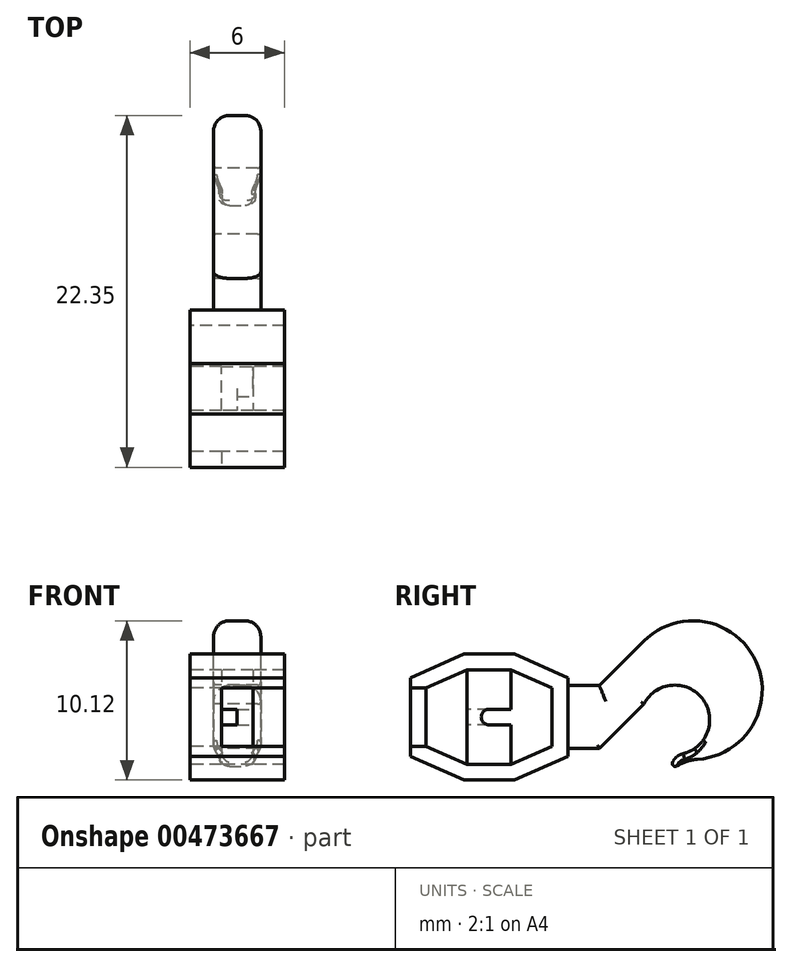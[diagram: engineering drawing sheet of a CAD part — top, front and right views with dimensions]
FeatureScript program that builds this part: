
annotation { "Feature Type Name" : "Feature", "Feature Type Description" : "" }
export const myFeature = defineFeature(function(context is Context, id is Id, definition is map)
    precondition{}
    {
        {
            var Q0;
            Q0=qCreatedBy(makeId("Right.planeOp"),FACE);
            var sketch = newSketch(context, id + "F0", { "sketchPlane" : qUnion([Q0])});
            skLineSegment(sketch, "E0", {"start": v(0, 0) * mm, "end": v(0, 4) * mm, "construction": true});
            skLineSegment(sketch, "E1", {"start": v(0, 0) * mm, "end": v(5, 0) * mm, "construction": true});
            skLineSegment(sketch, "E2", {"start": v(0, 4) * mm, "end": v(1.6, 4) * mm});
            skLineSegment(sketch, "E3", {"start": v(5, 0) * mm, "end": v(5, 2.5) * mm});
            skLineSegment(sketch, "E4", {"start": v(1.6, 4) * mm, "end": v(5, 2.5) * mm});
            skLineSegment(sketch, "E5.MirrorCS", {"start": v(0, 4) * mm, "end": v(-1.6, 4) * mm});
            skLineSegment(sketch, "E6.MirrorCS", {"start": v(-1.6, 4) * mm, "end": v(-5, 2.5) * mm});
            skLineSegment(sketch, "E7.MirrorCS", {"start": v(-5, 0) * mm, "end": v(-5, 2.5) * mm});
            skLineSegment(sketch, "E8.MirrorCS", {"start": v(-5, 0) * mm, "end": v(-5, -2.5) * mm});
            skLineSegment(sketch, "E9.MirrorCS", {"start": v(-1.6, -4) * mm, "end": v(-5, -2.5) * mm});
            skLineSegment(sketch, "E10.MirrorCS", {"start": v(0, -4) * mm, "end": v(1.6, -4) * mm});
            skLineSegment(sketch, "E11.MirrorCS", {"start": v(0, -4) * mm, "end": v(-1.6, -4) * mm});
            skLineSegment(sketch, "E12.MirrorCS", {"start": v(1.6, -4) * mm, "end": v(5, -2.5) * mm});
            skLineSegment(sketch, "E13.MirrorCS", {"start": v(5, 0) * mm, "end": v(5, -2.5) * mm});
            skLineSegment(sketch, "E14.0", {"start": v(0, 3) * mm, "end": v(1.39, 3) * mm});
            skLineSegment(sketch, "E14.1", {"start": v(0, -3) * mm, "end": v(1.39, -3) * mm});
            skLineSegment(sketch, "E14.2", {"start": v(1.39, -3) * mm, "end": v(4, -1.85) * mm});
            skLineSegment(sketch, "E14.3", {"start": v(4, 0) * mm, "end": v(4, -1.85) * mm});
            skLineSegment(sketch, "E14.4", {"start": v(4, 0) * mm, "end": v(4, 1.85) * mm});
            skLineSegment(sketch, "E14.5", {"start": v(0, -3) * mm, "end": v(-1.39, -3) * mm});
            skLineSegment(sketch, "E14.6", {"start": v(1.39, 3) * mm, "end": v(4, 1.85) * mm});
            skLineSegment(sketch, "E14.7", {"start": v(-1.39, -3) * mm, "end": v(-4, -1.85) * mm});
            skLineSegment(sketch, "E14.8", {"start": v(-4, 0) * mm, "end": v(-4, -1.85) * mm});
            skLineSegment(sketch, "E14.9", {"start": v(-4, 0) * mm, "end": v(-4, 1.85) * mm});
            skLineSegment(sketch, "E14.10", {"start": v(-1.39, 3) * mm, "end": v(-4, 1.85) * mm});
            skLineSegment(sketch, "E14.11", {"start": v(0, 3) * mm, "end": v(-1.39, 3) * mm});
            skSolve(sketch);
        }
        {
            var Q0;
            Q0=makeQuery(id+"F0.imprint","IMPRINT",FACE,{"disambiguationData":[TD([[makeQuery(id+"F0.imprint","IMPRINT",EDGE,{"derivedFrom":sQuery(id+"F0.wireOp",EDGE,"E14.0")}),-1.0]])]});
            var sketch = newSketch(context, id + "F1", { "sketchPlane" : qUnion([Q0])});
            skPoint(sketch, "E15.0", {"position": v(-1.39, 3) * mm});
            skPoint(sketch, "E16.0", {"position": v(1.39, 3) * mm});
            skPoint(sketch, "E17.0", {"position": v(-1.39, -3) * mm});
            skPoint(sketch, "E18.0", {"position": v(1.39, -3) * mm});
            skLineSegment(sketch, "E19.bottom", {"start": v(-1.39, 3) * mm, "end": v(1.39, 3) * mm});
            skLineSegment(sketch, "E19.top", {"start": v(-1.39, -3) * mm, "end": v(1.39, -3) * mm});
            skLineSegment(sketch, "E19.left", {"start": v(-1.39, 3) * mm, "end": v(-1.39, -3) * mm});
            skLineSegment(sketch, "E19.right", {"start": v(1.39, 3) * mm, "end": v(1.39, -3) * mm});
            skSolve(sketch);
        }
        {
            var Q0;
            Q0=qCreatedBy(makeId("Right.planeOp"),FACE);
            var sketch = newSketch(context, id + "F2", { "sketchPlane" : qUnion([Q0])});
            skPoint(sketch, "E20.0", {"position": v(5, 0) * mm});
            skLineSegment(sketch, "E21", {"start": v(5, 0) * mm, "end": v(5, 2) * mm, "construction": true});
            skLineSegment(sketch, "E22.bottom", {"start": v(5, 2) * mm, "end": v(7, 2) * mm});
            skLineSegment(sketch, "E22.top", {"start": v(5, -2) * mm, "end": v(7, -2) * mm});
            skLineSegment(sketch, "E22.left", {"start": v(5, 2) * mm, "end": v(5, -2) * mm});
            skLineSegment(sketch, "E22.right", {"start": v(7, 2) * mm, "end": v(7, -2) * mm});
            skLineSegment(sketch, "E23", {"start": v(5, 0) * mm, "end": v(17, 0) * mm, "construction": true});
            skLineSegment(sketch, "E24", {"start": v(7, 2) * mm, "end": v(9.83, 4.83) * mm});
            skLineSegment(sketch, "E25", {"start": v(7, -2) * mm, "end": v(9.83, 0.83) * mm});
            skArc(sketch, "E26", {"start": v(9.83, 4.83) * mm, "mid": v(15.4, 5.37) * mm, "end": v(17, 0) * mm});
            skLineSegment(sketch, "E27", {"start": v(17, 0) * mm, "end": v(14, 0) * mm, "construction": true});
            skArc(sketch, "E28", {"start": v(14, 0) * mm, "mid": v(12.23, 2) * mm, "end": v(9.83, 0.83) * mm});
            skArc(sketch, "E29", {"start": v(14, 0) * mm, "mid": v(13.58, -1.48) * mm, "end": v(12.3, -2.33) * mm});
            skArc(sketch, "E30", {"start": v(17, 0) * mm, "mid": v(15.5, -1.87) * mm, "end": v(13.25, -2.68) * mm});
            skLineSegment(sketch, "E31", {"start": v(14, 0) * mm, "end": v(13.25, 0) * mm, "construction": true});
            skLineSegment(sketch, "E32", {"start": v(13.25, 0) * mm, "end": v(12.3, 0) * mm, "construction": true});
            skLineSegment(sketch, "E33", {"start": v(13.25, -2.68) * mm, "end": v(13.25, -3.38) * mm, "construction": true});
            skArc(sketch, "E34", {"start": v(12.3, -2.33) * mm, "mid": v(11.73, -2.71) * mm, "end": v(11.56, -3.38) * mm});
            skArc(sketch, "E35", {"start": v(13.25, -2.68) * mm, "mid": v(12.35, -2.9) * mm, "end": v(11.56, -3.38) * mm});
            skLineSegment(sketch, "E36", {"start": v(13.25, -3.38) * mm, "end": v(11.56, -3.38) * mm, "construction": true});
            skSolve(sketch);
        }
        {
            var Q0;
            Q0=makeQuery(id+"F0.imprint","IMPRINT",FACE,{"disambiguationData":[TD([[makeQuery(id+"F0.imprint","IMPRINT",EDGE,{"derivedFrom":sQuery(id+"F0.wireOp",EDGE,"E2")}),-1.0]])]});
            extrude(context, id + "F3", {"entities" : qUnion([Q0]), "endBound" : BoundingType.SYMMETRIC, "depth" : 6 * mm});
        }
        {
            var Q0;
            {var subQ3=sQuery(id+"F1.wireOp",EDGE,"E19.left");Q0=makeQuery(id+"F1.imprint","IMPRINT",FACE,{"disambiguationData":[TD([[makeQuery(id+"F1.imprint","IMPRINT",EDGE,{"derivedFrom":subQ3}),1.0]])]});}
            extrude(context, id + "F4", {"entities" : qUnion([Q0]), "operationType" : NewBodyOperationType.ADD, "endBound" : BoundingType.SYMMETRIC, "depth" : 2 * mm});
        }
        {
            var Q0;
            Q0=makeQuery(id+"F2.imprint","IMPRINT",FACE,{"disambiguationData":[TD([[makeQuery(id+"F2.imprint","IMPRINT",EDGE,{"derivedFrom":sQuery(id+"F2.wireOp",EDGE,"E22.bottom")}),-1.0]])]});
            var Q1;
            Q1=makeQuery(id+"F2.imprint","IMPRINT",FACE,{"disambiguationData":[TD([[makeQuery(id+"F2.imprint","IMPRINT",EDGE,{"derivedFrom":sQuery(id+"F2.wireOp",EDGE,"E22.right")}),1.0]])]});
            extrude(context, id + "F5", {"entities" : qUnion([Q0, Q1]), "operationType" : NewBodyOperationType.ADD, "endBound" : BoundingType.SYMMETRIC, "depth" : 3 * mm});
        }
        {
            var Q0;
            Q0=makeQuery(id+"F3.opExtrude","CAP_FACE",FACE,{"disambiguationData":[OSD([sQuery(id+"F0.wireOp",EDGE,"E2"),sQuery(id+"F0.wireOp",EDGE,"E3"),sQuery(id+"F0.wireOp",EDGE,"E4"),sQuery(id+"F0.wireOp",EDGE,"E5.MirrorCS"),sQuery(id+"F0.wireOp",EDGE,"E6.MirrorCS"),sQuery(id+"F0.wireOp",EDGE,"E7.MirrorCS"),sQuery(id+"F0.wireOp",EDGE,"E8.MirrorCS"),sQuery(id+"F0.wireOp",EDGE,"E9.MirrorCS"),sQuery(id+"F0.wireOp",EDGE,"E10.MirrorCS"),sQuery(id+"F0.wireOp",EDGE,"E11.MirrorCS"),sQuery(id+"F0.wireOp",EDGE,"E12.MirrorCS"),sQuery(id+"F0.wireOp",EDGE,"E13.MirrorCS"),sQuery(id+"F0.wireOp",EDGE,"E14.0"),sQuery(id+"F0.wireOp",EDGE,"E14.1"),sQuery(id+"F0.wireOp",EDGE,"E14.2"),sQuery(id+"F0.wireOp",EDGE,"E14.3"),sQuery(id+"F0.wireOp",EDGE,"E14.4"),sQuery(id+"F0.wireOp",EDGE,"E14.5"),sQuery(id+"F0.wireOp",EDGE,"E14.6"),sQuery(id+"F0.wireOp",EDGE,"E14.7"),sQuery(id+"F0.wireOp",EDGE,"E14.8"),sQuery(id+"F0.wireOp",EDGE,"E14.9"),sQuery(id+"F0.wireOp",EDGE,"E14.10"),sQuery(id+"F0.wireOp",EDGE,"E14.11")])],"isStart":false});
            var sketch = newSketch(context, id + "F6", { "sketchPlane" : qUnion([Q0])});
            skPoint(sketch, "E37.0", {"position": v(-4, 1.85) * mm});
            skPoint(sketch, "E38.0", {"position": v(-5, 2.5) * mm});
            skPoint(sketch, "E39.0", {"position": v(-4, -1.85) * mm});
            skLineSegment(sketch, "E40.bottom", {"start": v(-4, 1.85) * mm, "end": v(-5, 1.85) * mm});
            skLineSegment(sketch, "E40.top", {"start": v(-4, -1.85) * mm, "end": v(-5, -1.85) * mm});
            skLineSegment(sketch, "E40.left", {"start": v(-4, 1.85) * mm, "end": v(-4, -1.85) * mm});
            skLineSegment(sketch, "E40.right", {"start": v(-5, 1.85) * mm, "end": v(-5, -1.85) * mm});
            skSolve(sketch);
        }
        {
            var Q0;
            Q0=makeQuery(id+"F6.imprint","IMPRINT",FACE,{"disambiguationData":[TD([[makeQuery(id+"F6.imprint","IMPRINT",EDGE,{"derivedFrom":sQuery(id+"F6.wireOp",EDGE,"E40.bottom")}),1.0]])]});
            extrude(context, id + "F7", {"entities" : qUnion([Q0]), "operationType" : NewBodyOperationType.REMOVE, "oppositeDirection" : true, "depth" : 4 * mm});
        }
        {
            var Q0;
            Q0=makeQuery(id+"F5.opExtrude","CAP_EDGE",EDGE,{"disambiguationData":[OSD([sQuery(id+"F2.wireOp",EDGE,"E22.bottom")])],"isStart":false});
            var Q1;
            Q1=makeQuery(id+"F5.opExtrude","CAP_EDGE",EDGE,{"disambiguationData":[OSD([sQuery(id+"F2.wireOp",EDGE,"E24")])],"isStart":false});
            var Q2;
            Q2=makeQuery(id+"F5.opExtrude","CAP_EDGE",EDGE,{"disambiguationData":[OSD([sQuery(id+"F2.wireOp",EDGE,"E26"),sQuery(id+"F2.wireOp",EDGE,"E30")])],"isStart":false});
            var Q3;
            Q3=makeQuery(id+"F5.opExtrude","CAP_EDGE",EDGE,{"disambiguationData":[OSD([sQuery(id+"F2.wireOp",EDGE,"E26"),sQuery(id+"F2.wireOp",EDGE,"E30")])],"isStart":true});
            var Q4;
            Q4=makeQuery(id+"F5.opExtrude","CAP_EDGE",EDGE,{"disambiguationData":[OSD([sQuery(id+"F2.wireOp",EDGE,"E22.bottom")])],"isStart":true});
            fillet(context, id + "F8", {"entities" : qUnion([Q0, Q1, Q2, Q3, Q4]), "radius" : 1 * mm, "tangentPropagation" : true, "allowEdgeOverflow" : false});
        }
        {
            var Q0;
            Q0=makeQuery(id+"F5.opExtrude","CAP_EDGE",EDGE,{"disambiguationData":[OSD([sQuery(id+"F2.wireOp",EDGE,"E28"),sQuery(id+"F2.wireOp",EDGE,"E29")])],"isStart":false});
            var Q1;
            Q1=makeQuery(id+"F5.opExtrude","CAP_EDGE",EDGE,{"disambiguationData":[OSD([sQuery(id+"F2.wireOp",EDGE,"E25")])],"isStart":false});
            var Q2;
            Q2=makeQuery(id+"F5.opExtrude","CAP_EDGE",EDGE,{"disambiguationData":[OSD([sQuery(id+"F2.wireOp",EDGE,"E22.top")])],"isStart":false});
            var Q3;
            Q3=makeQuery(id+"F5.opExtrude","CAP_EDGE",EDGE,{"disambiguationData":[OSD([sQuery(id+"F2.wireOp",EDGE,"E25")])],"isStart":true});
            var Q4;
            Q4=makeQuery(id+"F5.opExtrude","CAP_EDGE",EDGE,{"disambiguationData":[OSD([sQuery(id+"F2.wireOp",EDGE,"E22.top")])],"isStart":true});
            fillet(context, id + "F9", {"entities" : qUnion([Q0, Q1, Q2, Q3, Q4]), "radius" : .2 * mm, "tangentPropagation" : true, "allowEdgeOverflow" : false});
        }
        {
            var Q0;
            Q0=makeQuery(id+"F4.opExtrude","CAP_FACE",FACE,{"disambiguationData":[OSD([sQuery(id+"F1.wireOp",EDGE,"E19.bottom"),sQuery(id+"F1.wireOp",EDGE,"E19.top"),sQuery(id+"F1.wireOp",EDGE,"E19.left"),sQuery(id+"F1.wireOp",EDGE,"E19.right")])],"isStart":false});
            var sketch = newSketch(context, id + "F10", { "sketchPlane" : qUnion([Q0])});
            skArc(sketch, "E41", {"start": v(0, 0.5) * mm, "mid": v(-0.5, 0) * mm, "end": v(0, -0.5) * mm});
            skLineSegment(sketch, "E42", {"start": v(0, 0) * mm, "end": v(0, 0.5) * mm, "construction": true});
            skLineSegment(sketch, "E43", {"start": v(0, 0.5) * mm, "end": v(1.39, 0.5) * mm});
            skLineSegment(sketch, "E44", {"start": v(0, -0.5) * mm, "end": v(1.39, -0.5) * mm});
            skLineSegment(sketch, "E45", {"start": v(1.39, -0.5) * mm, "end": v(1.39, 0.5) * mm});
            skSolve(sketch);
        }
        {
            var Q0;
            Q0=makeQuery(id+"F10.imprint","IMPRINT",FACE,{"disambiguationData":[TD([[makeQuery(id+"F10.imprint","IMPRINT",EDGE,{"derivedFrom":sQuery(id+"F10.wireOp",EDGE,"E41")}),1.0]])]});
            extrude(context, id + "F11", {"entities" : qUnion([Q0]), "operationType" : NewBodyOperationType.REMOVE, "endBound" : BoundingType.THROUGH_ALL, "oppositeDirection" : true, "depth" : 25 * mm});
        }
        {
            var Q0;
            Q0=makeQuery(id+"F4.opExtrude","CAP_FACE",FACE,{"disambiguationData":[OSD([sQuery(id+"F1.wireOp",EDGE,"E19.bottom"),sQuery(id+"F1.wireOp",EDGE,"E19.top"),sQuery(id+"F1.wireOp",EDGE,"E19.left"),sQuery(id+"F1.wireOp",EDGE,"E19.right")])],"isStart":true});
            var sketch = newSketch(context, id + "F12", { "sketchPlane" : qUnion([Q0])});
            skPoint(sketch, "E46.0", {"position": v(0, 0.5) * mm});
            skPoint(sketch, "E47.0", {"position": v(0, -0.5) * mm});
            skLineSegment(sketch, "E48.bottom", {"start": v(0, 0.5) * mm, "end": v(1.39, 0.5) * mm});
            skLineSegment(sketch, "E48.top", {"start": v(0, -0.5) * mm, "end": v(1.39, -0.5) * mm});
            skLineSegment(sketch, "E48.left", {"start": v(0, 0.5) * mm, "end": v(0, -0.5) * mm});
            skLineSegment(sketch, "E48.right", {"start": v(1.39, 0.5) * mm, "end": v(1.39, -0.5) * mm});
            skSolve(sketch);
        }
        {
            var Q0;
            Q0=makeQuery(id+"F12.imprint","IMPRINT",FACE,{"disambiguationData":[TD([[makeQuery(id+"F12.imprint","IMPRINT",EDGE,{"derivedFrom":sQuery(id+"F12.wireOp",EDGE,"E48.bottom")}),-1.0]])]});
            extrude(context, id + "F13", {"entities" : qUnion([Q0]), "operationType" : NewBodyOperationType.REMOVE, "oppositeDirection" : true, "depth" : 1 * mm});
        }
    });
